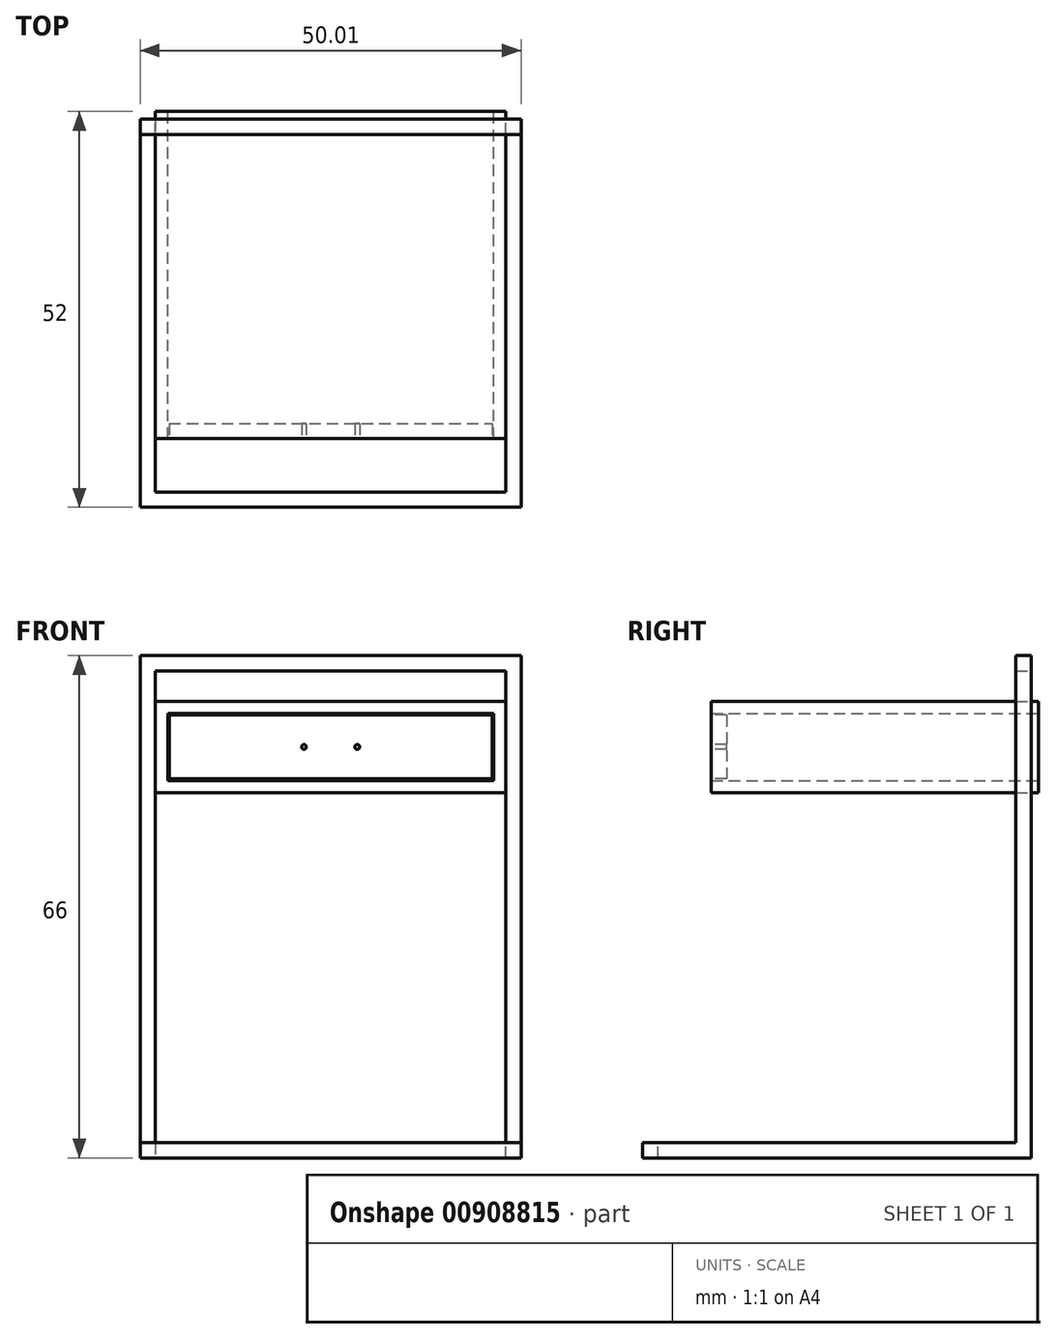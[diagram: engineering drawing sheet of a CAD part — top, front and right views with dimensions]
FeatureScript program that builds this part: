
annotation { "Feature Type Name" : "Feature", "Feature Type Description" : "" }
export const myFeature = defineFeature(function(context is Context, id is Id, definition is map)
    precondition{}
    {
        {
            var Q0;
            Q0=qCreatedBy(makeId("Front.planeOp"),FACE);
            var sketch = newSketch(context, id + "F0", { "sketchPlane" : qUnion([Q0])});
            skLineSegment(sketch, "E0.bottom", {"start": v(-142, 32.65) * mm, "end": v(-96, 32.65) * mm});
            skLineSegment(sketch, "E0.top", {"start": v(-142, 20.65) * mm, "end": v(-96, 20.65) * mm});
            skLineSegment(sketch, "E0.left", {"start": v(-142, 32.65) * mm, "end": v(-142, 20.65) * mm});
            skLineSegment(sketch, "E0.right", {"start": v(-96, 32.65) * mm, "end": v(-96, 20.65) * mm});
            skLineSegment(sketch, "E1.bottom", {"start": v(-140.4, 31.05) * mm, "end": v(-97.6, 31.05) * mm});
            skLineSegment(sketch, "E1.top", {"start": v(-140.4, 22.25) * mm, "end": v(-97.6, 22.25) * mm});
            skLineSegment(sketch, "E1.left", {"start": v(-140.4, 31.05) * mm, "end": v(-140.4, 22.25) * mm});
            skLineSegment(sketch, "E1.right", {"start": v(-97.6, 31.05) * mm, "end": v(-97.6, 22.25) * mm});
            skLineSegment(sketch, "E2", {"start": v(-97.6, 31.05) * mm, "end": v(-97.6, 32.65) * mm, "construction": true});
            skLineSegment(sketch, "E3", {"start": v(-97.6, 31.05) * mm, "end": v(-96, 31.05) * mm, "construction": true});
            skLineSegment(sketch, "E4", {"start": v(-97.6, 22.25) * mm, "end": v(-96, 22.25) * mm, "construction": true});
            skLineSegment(sketch, "E5", {"start": v(-97.6, 22.25) * mm, "end": v(-97.6, 20.65) * mm, "construction": true});
            skLineSegment(sketch, "E6", {"start": v(-140.4, 31.05) * mm, "end": v(-140.4, 32.65) * mm, "construction": true});
            skLineSegment(sketch, "E7", {"start": v(-140.4, 32.65) * mm, "end": v(-140.4, 31.05) * mm, "construction": true});
            skLineSegment(sketch, "E8", {"start": v(-140.4, 31.05) * mm, "end": v(-142, 31.05) * mm, "construction": true});
            skLineSegment(sketch, "E9", {"start": v(-140.4, 22.25) * mm, "end": v(-140.4, 20.65) * mm, "construction": true});
            skLineSegment(sketch, "E10", {"start": v(-140.4, 22.25) * mm, "end": v(-142, 22.25) * mm, "construction": true});
            skSolve(sketch);
        }
        {
            var Q0;
            Q0 = qSketchRegion(id + "F0", true);
            extrude(context, id + "F1", {"entities" : qUnion([Q0]), "depth" : 43 * mm, "offsetDistance" : 25 * mm});
        }
        {
            var Q0;
            Q0=makeQuery(id+"F1.opExtrude","SWEPT_FACE",FACE,{"disambiguationData":[OSD([sQuery(id+"F0.wireOp",EDGE,"E0.right")])]});
            var sketch = newSketch(context, id + "F2", { "sketchPlane" : qUnion([Q0])});
            skLineSegment(sketch, "E11.bottom", {"start": v(-43, 32.65) * mm, "end": v(0, 32.65) * mm});
            skLineSegment(sketch, "E11.top", {"start": v(-43, 20.65) * mm, "end": v(0, 20.65) * mm});
            skLineSegment(sketch, "E11.left", {"start": v(-43, 32.65) * mm, "end": v(-43, 20.65) * mm});
            skLineSegment(sketch, "E11.right", {"start": v(0, 32.65) * mm, "end": v(0, 20.65) * mm});
            skLineSegment(sketch, "E12", {"start": v(-1, 32.65) * mm, "end": v(-1, 20.65) * mm, "construction": true});
            skLineSegment(sketch, "E13", {"start": v(-3, 32.65) * mm, "end": v(-3, 20.65) * mm, "construction": true});
            skLineSegment(sketch, "E14", {"start": v(-3, 29.65) * mm, "end": v(-1, 29.65) * mm, "construction": true});
            skPoint(sketch, "E15", {"position": v(-2, 29.65) * mm});
            skCircle(sketch, "E16", {"center": v(-2, 29.65) * mm, "radius": 0.15 * mm});
            skLineSegment(sketch, "E17", {"start": v(-3, 23.65) * mm, "end": v(-1, 23.65) * mm, "construction": true});
            skPoint(sketch, "E18", {"position": v(-2, 23.65) * mm});
            skCircle(sketch, "E19", {"center": v(-2, 23.65) * mm, "radius": 0.15 * mm});
            skSolve(sketch);
        }
        {
            var Q0;
            Q0=makeQuery(id+"F1.opExtrude","CAP_FACE",FACE,{"disambiguationData":[OSD([sQuery(id+"F0.wireOp",EDGE,"E0.bottom"),sQuery(id+"F0.wireOp",EDGE,"E0.top"),sQuery(id+"F0.wireOp",EDGE,"E0.left"),sQuery(id+"F0.wireOp",EDGE,"E0.right"),sQuery(id+"F0.wireOp",EDGE,"E1.bottom"),sQuery(id+"F0.wireOp",EDGE,"E1.top"),sQuery(id+"F0.wireOp",EDGE,"E1.left"),sQuery(id+"F0.wireOp",EDGE,"E1.right")])],"isStart":false});
            var sketch = newSketch(context, id + "F3", { "sketchPlane" : qUnion([Q0])});
            skLineSegment(sketch, "E20.bottom", {"start": v(-140.2, 30.85) * mm, "end": v(-97.8, 30.85) * mm});
            skLineSegment(sketch, "E20.top", {"start": v(-140.2, 22.45) * mm, "end": v(-97.8, 22.45) * mm});
            skLineSegment(sketch, "E20.left", {"start": v(-140.2, 30.85) * mm, "end": v(-140.2, 22.45) * mm});
            skLineSegment(sketch, "E20.right", {"start": v(-97.8, 30.85) * mm, "end": v(-97.8, 22.45) * mm});
            skLineSegment(sketch, "E21", {"start": v(-140.2, 30.85) * mm, "end": v(-97.8, 22.45) * mm, "construction": true});
            skLineSegment(sketch, "E22", {"start": v(-97.8, 30.85) * mm, "end": v(-140.2, 22.45) * mm, "construction": true});
            skPoint(sketch, "E23", {"position": v(-119, 26.65) * mm});
            skLineSegment(sketch, "E24", {"start": v(-119, 26.65) * mm, "end": v(-115.5, 26.65) * mm, "construction": true});
            skLineSegment(sketch, "E25", {"start": v(-119, 26.65) * mm, "end": v(-122.5, 26.65) * mm, "construction": true});
            skCircle(sketch, "E26", {"center": v(-115.5, 26.65) * mm, "radius": 0.31 * mm});
            skLineSegment(sketch, "E27", {"start": v(-119, 26.65) * mm, "end": v(-119, 41.8) * mm, "construction": true});
            skLineSegment(sketch, "E28", {"start": v(-119, 41.8) * mm, "end": v(-119, 26.65) * mm, "construction": true});
            skLineSegment(sketch, "E29", {"start": v(-119, 17.41) * mm, "end": v(-119, 26.65) * mm, "construction": true});
            skCircle(sketch, "E30.MirrorC", {"center": v(-122.5, 26.65) * mm, "radius": 0.31 * mm});
            skSolve(sketch);
        }
        {
            var Q0;
            Q0 = qSketchRegion(id + "F3", true);
            extrude(context, id + "F4", {"entities" : qUnion([Q0]), "oppositeDirection" : true, "depth" : 2 * mm, "offsetDistance" : 25 * mm});
        }
        {
            var Q0;
            Q0=makeQuery(id+"F2.imprint","IMPRINT",FACE,{"disambiguationData":[TD([[makeQuery(id+"F2.imprint","IMPRINT",EDGE,{"derivedFrom":sQuery(id+"F2.wireOp",EDGE,"E11.bottom")}),-1.0]])]});
            cPlane(context, id + "F5", {"entities" : qUnion([Q0]), "cplaneType" : CPlaneType.OFFSET, "offset" : 0.01 * mm, "width" : 150 * mm, "height" : 150 * mm});
        }
        {
            var Q0;
            Q0=makeQuery(id+"F1.opExtrude","SWEPT_FACE",FACE,{"disambiguationData":[OSD([sQuery(id+"F0.wireOp",EDGE,"E0.left")])]});
            cPlane(context, id + "F6", {"entities" : qUnion([Q0]), "cplaneType" : CPlaneType.OFFSET, "offset" : 0 * mm, "width" : 150 * mm, "height" : 150 * mm});
        }
        {
            var Q0;
            Q0=qCreatedBy(id+"F5.planeOp",FACE);
            var sketch = newSketch(context, id + "F7", { "sketchPlane" : qUnion([Q0])});
            skLineSegment(sketch, "E31", {"start": v(-1, 38.65) * mm, "end": v(-1, -27.35) * mm});
            skLineSegment(sketch, "E32", {"start": v(-1, -27.35) * mm, "end": v(-50, -27.35) * mm});
            skLineSegment(sketch, "E33", {"start": v(-50, -27.35) * mm, "end": v(-50, -25.35) * mm});
            skLineSegment(sketch, "E34", {"start": v(-50, -25.35) * mm, "end": v(-3, -25.35) * mm});
            skLineSegment(sketch, "E35", {"start": v(-3, -25.35) * mm, "end": v(-3, 38.65) * mm});
            skLineSegment(sketch, "E36", {"start": v(-3, 38.65) * mm, "end": v(-1, 38.65) * mm});
            skLineSegment(sketch, "E37", {"start": v(-43, 31.36) * mm, "end": v(-43, 10.03) * mm, "construction": true});
            skSolve(sketch);
        }
        {
            var Q0;
            Q0 = qSketchRegion(id + "F7", true);
            extrude(context, id + "F8", {"entities" : qUnion([Q0]), "depth" : 2 * mm, "offsetDistance" : 25 * mm});
        }
        {
            var Q0;
            Q0=qCreatedBy(id+"F6.planeOp",FACE);
            var sketch = newSketch(context, id + "F9", { "sketchPlane" : qUnion([Q0])});
            skLineSegment(sketch, "E38", {"start": v(1, 38.65) * mm, "end": v(3, 38.65) * mm});
            skLineSegment(sketch, "E39", {"start": v(3, 38.65) * mm, "end": v(3, -25.35) * mm});
            skLineSegment(sketch, "E40", {"start": v(3, -25.35) * mm, "end": v(50, -25.35) * mm});
            skLineSegment(sketch, "E41", {"start": v(50, -25.35) * mm, "end": v(50, -27.35) * mm});
            skLineSegment(sketch, "E42", {"start": v(50, -27.35) * mm, "end": v(1, -27.35) * mm});
            skLineSegment(sketch, "E43", {"start": v(1, -27.35) * mm, "end": v(1, 38.65) * mm});
            skSolve(sketch);
        }
        {
            var Q0;
            Q0 = qSketchRegion(id + "F9", true);
            extrude(context, id + "F10", {"entities" : qUnion([Q0]), "depth" : 2 * mm, "offsetDistance" : 25 * mm});
        }
        {
            var Q0;
            Q0=makeQuery(id+"F8.opExtrude","SWEPT_FACE",FACE,{"disambiguationData":[OSD([sQuery(id+"F7.wireOp",EDGE,"E31")])]});
            var sketch = newSketch(context, id + "F11", { "sketchPlane" : qUnion([Q0])});
            skLineSegment(sketch, "E44.bottom", {"start": v(93.99, 38.65) * mm, "end": v(144, 38.65) * mm});
            skLineSegment(sketch, "E44.top", {"start": v(93.99, 36.65) * mm, "end": v(144, 36.65) * mm});
            skLineSegment(sketch, "E44.left", {"start": v(93.99, 38.65) * mm, "end": v(93.99, 36.65) * mm});
            skLineSegment(sketch, "E44.right", {"start": v(144, 38.65) * mm, "end": v(144, 36.65) * mm});
            skSolve(sketch);
        }
        {
            var Q0;
            Q0 = qSketchRegion(id + "F11", true);
            extrude(context, id + "F12", {"entities" : qUnion([Q0]), "operationType" : NewBodyOperationType.ADD, "oppositeDirection" : true, "depth" : 2 * mm, "offsetDistance" : 25 * mm});
        }
        {
            var Q0;
            Q0=makeQuery(id+"F10.opExtrude","SWEPT_FACE",FACE,{"disambiguationData":[OSD([sQuery(id+"F9.wireOp",EDGE,"E41")])]});
            var sketch = newSketch(context, id + "F13", { "sketchPlane" : qUnion([Q0])});
            skLineSegment(sketch, "E45.bottom", {"start": v(-144, -25.35) * mm, "end": v(-93.99, -25.35) * mm});
            skLineSegment(sketch, "E45.top", {"start": v(-144, -27.35) * mm, "end": v(-93.99, -27.35) * mm});
            skLineSegment(sketch, "E45.left", {"start": v(-144, -25.35) * mm, "end": v(-144, -27.35) * mm});
            skLineSegment(sketch, "E45.right", {"start": v(-93.99, -25.35) * mm, "end": v(-93.99, -27.35) * mm});
            skSolve(sketch);
        }
        {
            var Q0;
            Q0 = qSketchRegion(id + "F13", true);
            extrude(context, id + "F14", {"entities" : qUnion([Q0]), "operationType" : NewBodyOperationType.ADD, "depth" : 2 * mm, "offsetDistance" : 25 * mm});
        }
    });
